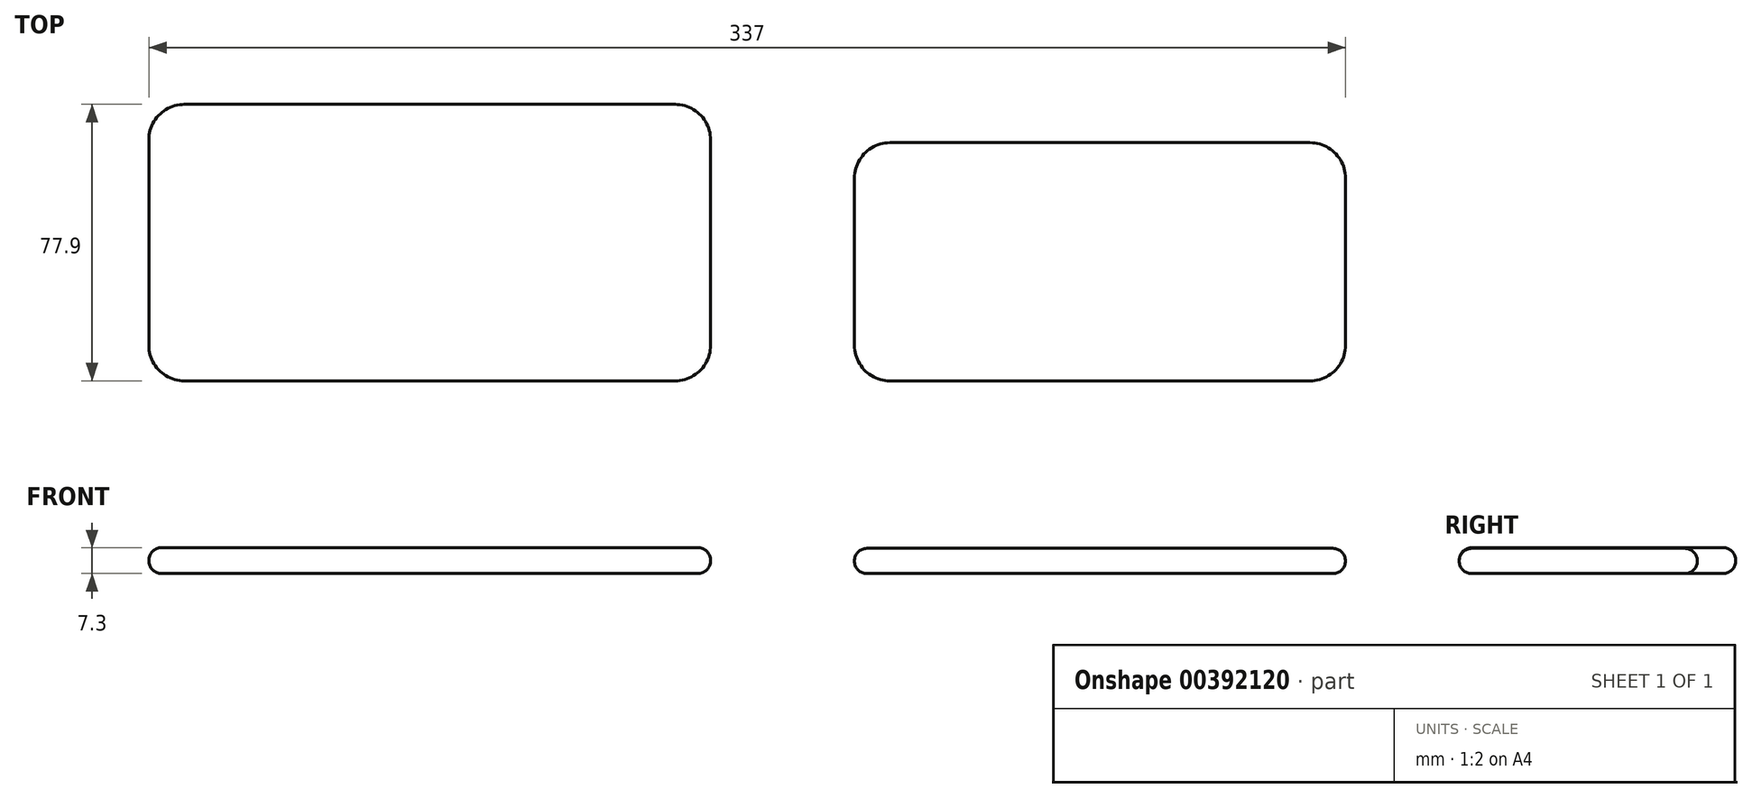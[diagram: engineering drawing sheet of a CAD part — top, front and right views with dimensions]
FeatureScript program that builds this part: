
annotation { "Feature Type Name" : "Feature", "Feature Type Description" : "" }
export const myFeature = defineFeature(function(context is Context, id is Id, definition is map)
    precondition{}
    {
        {
            var Q0;
            Q0=qCreatedBy(makeId("Top.planeOp"),FACE);
            var sketch = newSketch(context, id + "F0", { "sketchPlane" : qUnion([Q0])});
            skLineSegment(sketch, "E0.bottom", {"start": v(40.5, 0) * mm, "end": v(178.8, 0) * mm});
            skLineSegment(sketch, "E0.top", {"start": v(40.5, 67.1) * mm, "end": v(178.8, 67.1) * mm});
            skLineSegment(sketch, "E0.left", {"start": v(40.5, 0) * mm, "end": v(40.5, 67.1) * mm});
            skLineSegment(sketch, "E0.right", {"start": v(178.8, 0) * mm, "end": v(178.8, 67.1) * mm});
            skSolve(sketch);
        }
        {
            var Q0;
            Q0=qCreatedBy(makeId("Top.planeOp"),FACE);
            var sketch = newSketch(context, id + "F1", { "sketchPlane" : qUnion([Q0])});
            skLineSegment(sketch, "E1.bottom", {"start": v(0, 0) * mm, "end": v(-158.2, 0) * mm});
            skLineSegment(sketch, "E1.top", {"start": v(0, 77.9) * mm, "end": v(-158.2, 77.9) * mm});
            skLineSegment(sketch, "E1.left", {"start": v(0, 0) * mm, "end": v(0, 77.9) * mm});
            skLineSegment(sketch, "E1.right", {"start": v(-158.2, 0) * mm, "end": v(-158.2, 77.9) * mm});
            skSolve(sketch);
        }
        {
            var Q0;
            Q0 = qSketchRegion(id + "F0", true);
            extrude(context, id + "F2", {"entities" : qUnion([Q0]), "depth" : 7.1 * mm});
        }
        {
            var Q0;
            Q0 = qSketchRegion(id + "F1", true);
            extrude(context, id + "F3", {"entities" : qUnion([Q0]), "depth" : 7.3 * mm});
        }
        {
            var Q0;
            Q0=makeQuery(id+"F2.opExtrude","SWEPT_EDGE",EDGE,{"disambiguationData":[OSD([sQuery(id+"F0.wireOp",EDGE,"E0.top"),sQuery(id+"F0.wireOp",EDGE,"E0.left")])]});
            var Q1;
            Q1=makeQuery(id+"F2.opExtrude","SWEPT_EDGE",EDGE,{"disambiguationData":[OSD([sQuery(id+"F0.wireOp",EDGE,"E0.bottom"),sQuery(id+"F0.wireOp",EDGE,"E0.left")])]});
            var Q2;
            Q2=makeQuery(id+"F2.opExtrude","SWEPT_EDGE",EDGE,{"disambiguationData":[OSD([sQuery(id+"F0.wireOp",EDGE,"E0.bottom"),sQuery(id+"F0.wireOp",EDGE,"E0.right")])]});
            var Q3;
            Q3=makeQuery(id+"F2.opExtrude","SWEPT_EDGE",EDGE,{"disambiguationData":[OSD([sQuery(id+"F0.wireOp",EDGE,"E0.top"),sQuery(id+"F0.wireOp",EDGE,"E0.right")])]});
            fillet(context, id + "F4", {"entities" : qUnion([Q0, Q1, Q2, Q3]), "radius" : 10 * mm, "tangentPropagation" : true, "allowEdgeOverflow" : false});
        }
        {
            var Q0;
            Q0=makeQuery(id+"F2.opExtrude","CAP_FACE",FACE,{"disambiguationData":[OSD([sQuery(id+"F0.wireOp",EDGE,"E0.bottom"),sQuery(id+"F0.wireOp",EDGE,"E0.top"),sQuery(id+"F0.wireOp",EDGE,"E0.left"),sQuery(id+"F0.wireOp",EDGE,"E0.right")])],"isStart":false});
            var Q1;
            Q1=makeQuery(id+"F2.opExtrude","CAP_FACE",FACE,{"disambiguationData":[OSD([sQuery(id+"F0.wireOp",EDGE,"E0.bottom"),sQuery(id+"F0.wireOp",EDGE,"E0.top"),sQuery(id+"F0.wireOp",EDGE,"E0.left"),sQuery(id+"F0.wireOp",EDGE,"E0.right")])],"isStart":true});
            fillet(context, id + "F5", {"entities" : qUnion([Q0, Q1]), "radius" : (7.1 / 2) * mm, "tangentPropagation" : true, "allowEdgeOverflow" : false});
        }
        {
            var Q0;
            Q0=makeQuery(id+"F3.opExtrude","SWEPT_EDGE",EDGE,{"disambiguationData":[OSD([sQuery(id+"F1.wireOp",EDGE,"E1.bottom"),sQuery(id+"F1.wireOp",EDGE,"E1.right")])]});
            var Q1;
            Q1=makeQuery(id+"F3.opExtrude","SWEPT_EDGE",EDGE,{"disambiguationData":[OSD([sQuery(id+"F1.wireOp",EDGE,"E1.top"),sQuery(id+"F1.wireOp",EDGE,"E1.right")])]});
            var Q2;
            Q2=makeQuery(id+"F3.opExtrude","SWEPT_EDGE",EDGE,{"disambiguationData":[OSD([sQuery(id+"F1.wireOp",EDGE,"E1.bottom"),sQuery(id+"F1.wireOp",EDGE,"E1.left")])]});
            var Q3;
            Q3=makeQuery(id+"F3.opExtrude","SWEPT_EDGE",EDGE,{"disambiguationData":[OSD([sQuery(id+"F1.wireOp",EDGE,"E1.top"),sQuery(id+"F1.wireOp",EDGE,"E1.left")])]});
            fillet(context, id + "F6", {"entities" : qUnion([Q0, Q1, Q2, Q3]), "radius" : 10 * mm, "tangentPropagation" : true, "allowEdgeOverflow" : false});
        }
        {
            var Q0;
            Q0=makeQuery(id+"F3.opExtrude","CAP_FACE",FACE,{"disambiguationData":[OSD([sQuery(id+"F1.wireOp",EDGE,"E1.bottom"),sQuery(id+"F1.wireOp",EDGE,"E1.top"),sQuery(id+"F1.wireOp",EDGE,"E1.left"),sQuery(id+"F1.wireOp",EDGE,"E1.right")])],"isStart":true});
            var Q1;
            Q1=makeQuery(id+"F3.opExtrude","CAP_FACE",FACE,{"disambiguationData":[OSD([sQuery(id+"F1.wireOp",EDGE,"E1.bottom"),sQuery(id+"F1.wireOp",EDGE,"E1.top"),sQuery(id+"F1.wireOp",EDGE,"E1.left"),sQuery(id+"F1.wireOp",EDGE,"E1.right")])],"isStart":false});
            fillet(context, id + "F7", {"entities" : qUnion([Q0, Q1]), "radius" : (7.3 / 2) * mm, "tangentPropagation" : true, "allowEdgeOverflow" : false});
        }
    });
